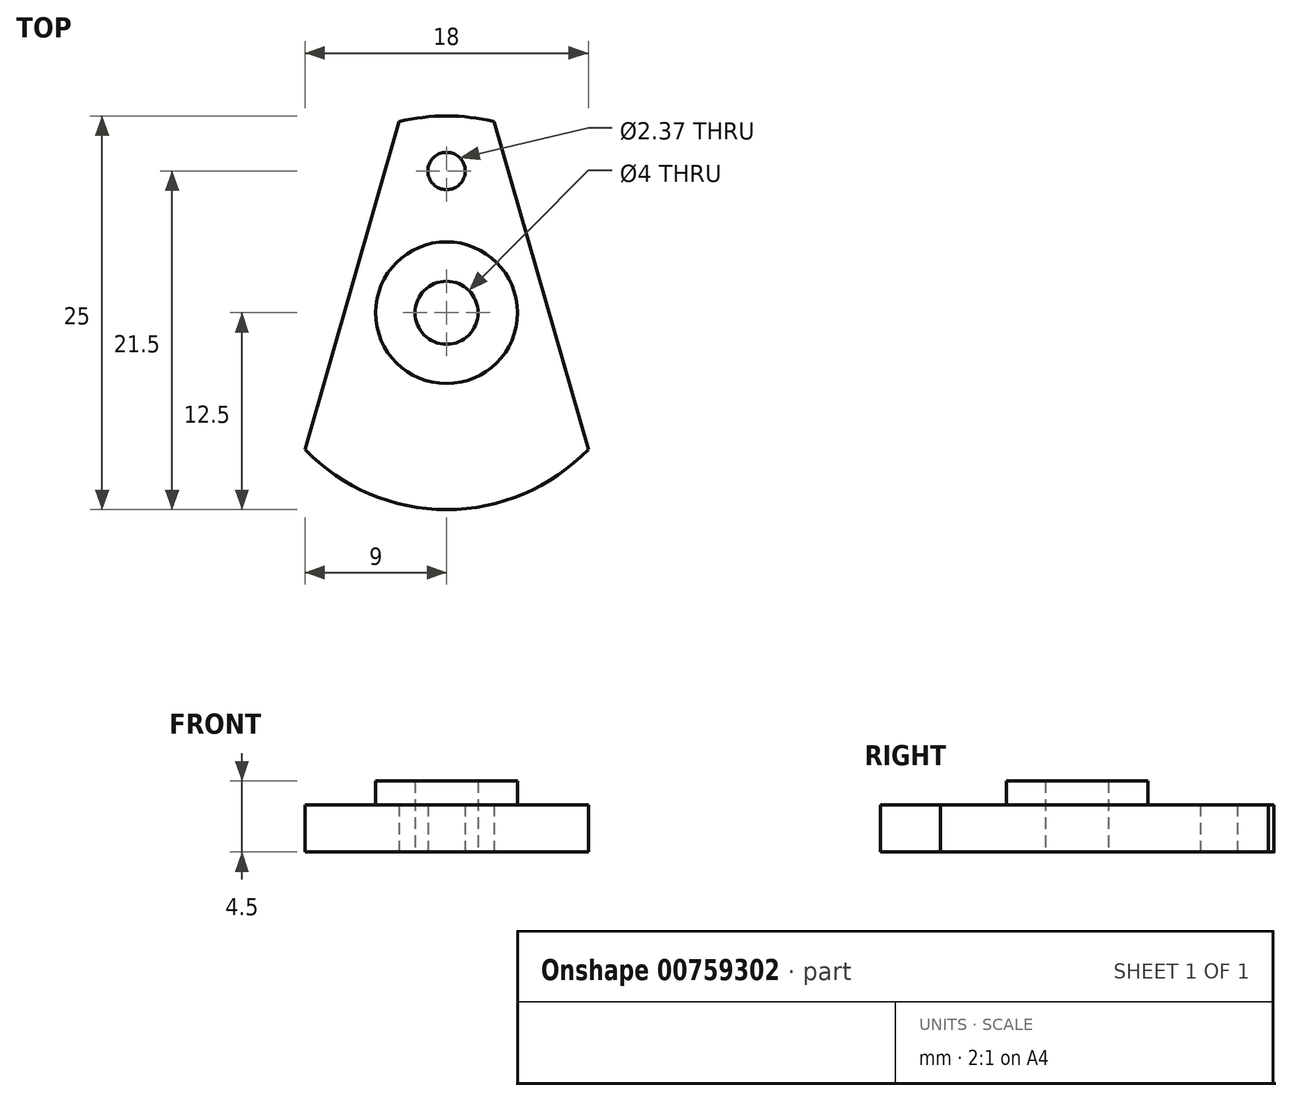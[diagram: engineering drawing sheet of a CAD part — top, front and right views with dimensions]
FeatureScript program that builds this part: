
annotation { "Feature Type Name" : "Feature", "Feature Type Description" : "" }
export const myFeature = defineFeature(function(context is Context, id is Id, definition is map)
    precondition{}
    {
        {
            var Q0;
            Q0=qCreatedBy(makeId("Top.planeOp"),FACE);
            var sketch = newSketch(context, id + "F0", { "sketchPlane" : qUnion([Q0])});
            skArc(sketch, "E0", {"start": v(-9, -8.67) * mm, "mid": v(0, -12.5) * mm, "end": v(9, -8.67) * mm});
            skLineSegment(sketch, "E1", {"start": v(0, 12.5) * mm, "end": v(0, 10.19) * mm});
            skLineSegment(sketch, "E2", {"start": v(3, 12.13) * mm, "end": v(9, -8.67) * mm});
            skLineSegment(sketch, "E3", {"start": v(-3, 12.13) * mm, "end": v(-9, -8.67) * mm});
            skArc(sketch, "E4.trimOffspring", {"start": v(3, 12.13) * mm, "mid": v(0, 12.5) * mm, "end": v(-3, 12.13) * mm});
            skCircle(sketch, "E5", {"center": v(0, 0) * mm, "radius": 4.5 * mm});
            skCircle(sketch, "E6", {"center": v(0, 0) * mm, "radius": 2 * mm});
            skCircle(sketch, "E7", {"center": v(0, 9) * mm, "radius": 1.19 * mm});
            skSolve(sketch);
        }
        {
            var Q0;
            Q0 = qSketchRegion(id + "F0", true);
            extrude(context, id + "F1", {"entities" : qUnion([Q0]), "depth" : 3 * mm, "offsetDistance" : 25 * mm});
        }
        {
            var Q0;
            Q0=makeQuery(id+"F0.imprint","IMPRINT",FACE,{"disambiguationData":[TD([[makeQuery(id+"F0.imprint","IMPRINT",EDGE,{"derivedFrom":sQuery(id+"F0.wireOp",EDGE,"E5")}),1.0]])]});
            var sketch = newSketch(context, id + "F2", { "sketchPlane" : qUnion([Q0])});
            skSolve(sketch);
        }
        {
            var Q0;
            Q0 = qSketchRegion(id + "F2", true);
            var Q1;
            Q1=makeQuery(id+"F2.imprint","IMPRINT",FACE,{"disambiguationData":[TD([[makeQuery(id+"F2.imprint","IMPRINT",EDGE,{"derivedFrom":makeQuery(id+"F0.imprint","IMPRINT",EDGE,{"derivedFrom":sQuery(id+"F0.wireOp",EDGE,"E5")})}),1.0]])]});
            extrude(context, id + "F3", {"entities" : qUnion([Q0, Q1]), "operationType" : NewBodyOperationType.ADD, "depth" : 4.5 * mm, "offsetDistance" : 25 * mm});
        }
    });
